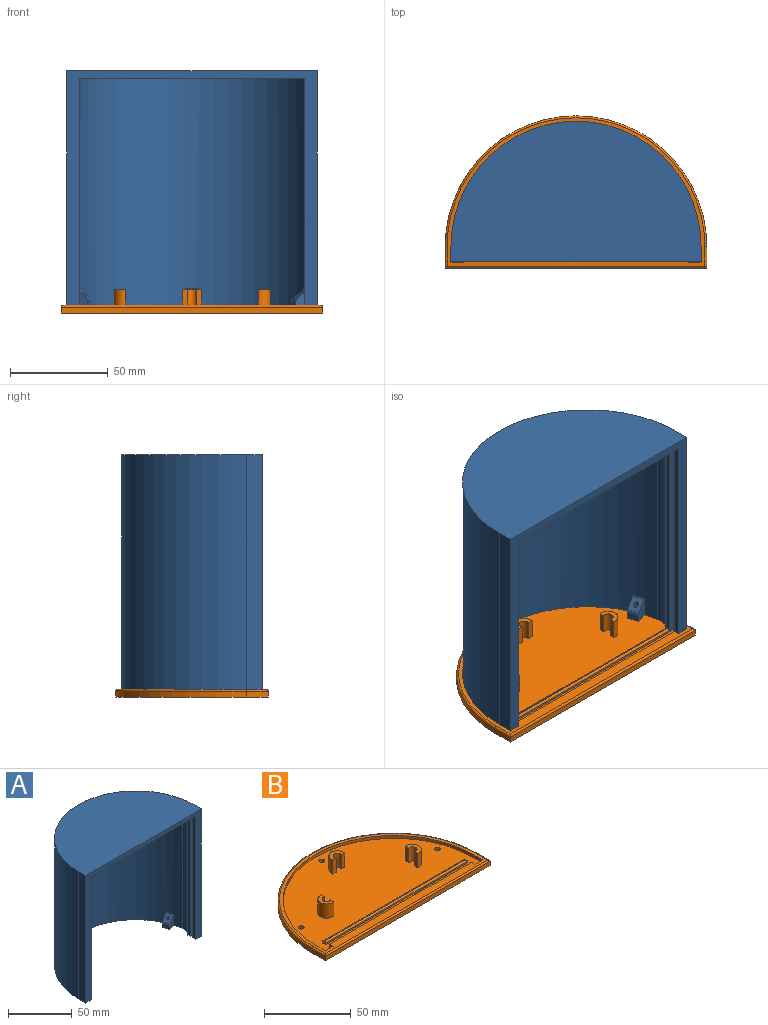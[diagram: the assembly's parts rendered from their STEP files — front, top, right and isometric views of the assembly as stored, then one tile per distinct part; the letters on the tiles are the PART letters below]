
ASSEMBLY  parts=2 mates=1
PART A: 43 faces, bbox 128x72x122 mm
  f0: plane 122.61x63.8mm, normal (0,0,-1), area 6215.1mm2, adj f4,f5,f6,f7,f8,f9,f10,f11
  f1: plane 115.5x3mm, normal (0,0,-1), area 346.5mm2, adj f2,f13,f14,f18
  f2: plane 118x3mm, normal (1,0,0), area 354mm2, adj f1,f13,f18,f20
  f3: plane 120x3.2mm, normal (1,0,0), area 384mm2, adj f11,f13,f20,f21
  f4: plane 118x2.33mm, normal (1,0,0), area 274.7mm2, adj f0,f5,f11,f20
  f5: plane 118x1.73mm, normal (0.78,0.62,0), area 261.1mm2, adj f0,f4,f6,f20
  f6: cylinder r=10mm len=118mm, axis (0,0,-1), area 986.5mm2, adj f0,f5,f7,f20
  f7: cylinder r=62mm len=122.34mm, axis (0,0,-1), area 20371.4mm2, adj f0,f6,f8,f20,f23,f25,f26,f28
  f8: cylinder r=10mm len=118mm, axis (0,0,-1), area 986.5mm2, adj f0,f7,f9,f20
  f9: plane 118x1.73mm, normal (-0.78,0.62,0), area 261.1mm2, adj f0,f8,f10,f20
  f10: plane 118x2.33mm, normal (-1,0,0), area 274.7mm2, adj f0,f9,f11,f20
  f11: plane 120.5x120mm, normal (0,-1,0), area 831mm2, adj f0,f3,f4,f10,f12,f20,f21
  f12: plane 120x3.2mm, normal (-1,0,0), area 384mm2, adj f11,f13,f20,f21
  f13: plane 120.5x120mm, normal (0,1,0), area 831mm2, adj f1,f2,f3,f12,f14,f20,f21
  f14: plane 118x3mm, normal (-1,0,0), area 354mm2, adj f1,f13,f18,f20
  f15: plane 122x8mm, normal (1,0,0), area 976mm2, adj f16,f18,f19,f20
  f16: cylinder r=64mm len=128mm, axis (0,0,-1), area 24529.6mm2, adj f15,f17,f19,f20
  f17: plane 122x8mm, normal (-1,0,0), area 976mm2, adj f16,f18,f19,f20
  f18: plane 128x122mm, normal (0,-1,0), area 1987mm2, adj f1,f2,f14,f15,f17,f19,f20
  f19: plane 128x72mm, normal (0,0,1), area 7458mm2, adj f15,f16,f17,f18
  f20: plane 128x72mm, normal (0,0,-1), area 623.9mm2, adj f2,f3,f4,f5,f6,f7,f8,f9
  f21: plane 120.5x3.2mm, normal (0,0,-1), area 385.6mm2, adj f3,f11,f12,f13
  f22: plane 7x4.16mm, normal (0,-1,0), area 28.6mm2, adj f20,f23,f25,f37
  f23: plane 10.48x5.92mm, normal (-1,0,0), area 44.4mm2, adj f7,f20,f22,f35,f37,f41
  f24: cylinder r=1.2mm len=8.5mm, axis (0,0,-1), area 57.5mm2, adj f20,f35
  f25: plane 10.48x5.92mm, normal (1,0,0), area 44.4mm2, adj f7,f20,f22,f35,f37,f41
  f26: plane 10.48x6.05mm, normal (0.34,-0.94,0), area 47mm2, adj f7,f20,f27,f34,f38,f40
  f27: plane 6.04x3.79mm, normal (-0.94,-0.34,0), area 23.9mm2, adj f20,f26,f28,f38
  f28: plane 10.48x6.04mm, normal (-0.34,0.94,0), area 47mm2, adj f7,f20,f27,f34,f38,f40
  f29: cylinder r=1.2mm len=8.5mm, axis (0,0,-1), area 56.7mm2, adj f20,f34
  f30: plane 6.58x4.36mm, normal (0.94,-0.34,0), area 29.2mm2, adj f20,f31,f33,f39
  f31: plane 10.48x5.77mm, normal (-0.34,-0.94,0), area 45.6mm2, adj f7,f20,f30,f36,f39,f42
  f32: cylinder r=1.2mm len=8.44mm, axis (0,0,-1), area 56.4mm2, adj f20,f36
  f33: plane 10.48x5.76mm, normal (0.34,0.94,0), area 45.6mm2, adj f7,f20,f30,f36,f39,f42
  f34: cone r=56mm half-angle=50.2deg, axis (0,0,1), area 41.6mm2, adj f26,f28,f29,f38,f40
  f35: cone r=56mm half-angle=50.2deg, axis (0,0,1), area 38.5mm2, adj f23,f24,f25,f37,f41
  f36: cone r=56mm half-angle=50.2deg, axis (0,0,1), area 45.6mm2, adj f31,f32,f33,f39,f42
  f37: bspline ~17.48x2.4mm, area 12.3mm2, adj f22,f23,f25,f35
  f38: bspline ~7.98x3.19mm, area 9mm2, adj f26,f27,f28,f34
  f39: bspline ~6.8x2.54mm, area 6mm2, adj f30,f31,f33,f36
  f40: torus R=61mm, axis (0,0,-1), area 5.6mm2, adj f7,f26,f28,f34
  f41: torus R=61mm, axis (0,0,-1), area 6.1mm2, adj f7,f23,f25,f35
  f42: torus R=61mm, axis (0,0,-1), area 6.1mm2, adj f7,f31,f33,f36
PART B: 46 faces, bbox 145x83.5x12 mm
  f0: plane 128x72mm, normal (0,0,1), area 6716.5mm2, adj f1,f2,f3,f10,f11,f12,f13,f14
  f1: cylinder r=1.6mm len=3.2mm, axis (0,0,-1), area 20.1mm2, adj f0,f9
  f2: cylinder r=1.6mm len=3.2mm, axis (0,0,-1), area 20.1mm2, adj f0,f9
  f3: cylinder r=1.6mm len=3.2mm, axis (0,0,-1), area 20.1mm2, adj f0,f9
  f4: plane 132x76mm, normal (0,0,1), area 1050.9mm2, adj f13,f14,f15,f16,f17,f18,f19,f21
  f5: plane 11x3mm, normal (1,0,0), area 33mm2, adj f6,f8,f9,f30
  f6: cylinder r=67mm len=134mm, axis (0,0,-1), area 631.5mm2, adj f5,f7,f9,f28
  f7: plane 11x3mm, normal (-1,0,0), area 33mm2, adj f6,f8,f9,f27
  f8: plane 134x3mm, normal (0,-1,0), area 402mm2, adj f5,f7,f9,f29
  f9: plane 134x78mm, normal (0,0,-1), area 8501.2mm2, adj f1,f2,f3,f5,f6,f7,f8
  f10: plane 115.5x1mm, normal (0,-1,0), area 115.5mm2, adj f0,f11,f20,f24
  f11: plane 2.33x1mm, normal (-1,0,0), area 2.3mm2, adj f0,f10,f12,f23
  f12: plane 115.5x1mm, normal (0,1,0), area 115.5mm2, adj f0,f11,f20,f25
  f13: plane 8x2mm, normal (-1,0,0), area 16mm2, adj f0,f4,f14,f21
  f14: cylinder r=64mm len=128mm, axis (0,0,1), area 402.1mm2, adj f0,f4,f13,f15
  f15: plane 8x2mm, normal (1,0,0), area 16mm2, adj f0,f4,f14,f16
  f16: plane 6.25x2mm, normal (0,1,0), area 12.5mm2, adj f0,f4,f15,f17
  f17: plane 3x2mm, normal (-1,0,0), area 6mm2, adj f0,f4,f16,f18
  f18: plane 115.5x2mm, normal (0,1,0), area 231mm2, adj f0,f4,f17,f19
  f19: plane 3x2mm, normal (1,0,0), area 6mm2, adj f0,f4,f18,f21
  f20: plane 2.33x1mm, normal (1,0,0), area 2.3mm2, adj f0,f10,f12,f26
  f21: plane 6.25x2mm, normal (0,1,0), area 12.5mm2, adj f0,f4,f13,f19
  f22: plane 113.5x0.33mm, normal (0,0,1), area 37.2mm2, adj f23,f24,f25,f26
  f23: cylinder r=1mm len=2.33mm, axis (0,-1,0), area 2.5mm2, adj f11,f22,f24,f25
  f24: cylinder r=1mm len=115.5mm, axis (1,0,0), area 180.3mm2, adj f10,f22,f23,f26
  f25: cylinder r=1mm len=115.5mm, axis (-1,0,0), area 180.3mm2, adj f12,f22,f23,f26
  f26: cylinder r=1mm len=2.33mm, axis (0,1,0), area 2.5mm2, adj f20,f22,f24,f25
  f27: cylinder r=1mm len=11mm, axis (0,1,0), area 16.7mm2, adj f4,f7,f28,f29
  f28: torus R=66mm, axis (0,0,1), area 328.8mm2, adj f4,f6,f27,f30
  f29: cylinder r=1mm len=134mm, axis (-1,0,0), area 209.3mm2, adj f4,f8,f27,f30
  f30: cylinder r=1mm len=11mm, axis (0,-1,0), area 16.7mm2, adj f4,f5,f28,f29
  f31: plane 10x2.55mm, normal (1,0,0), area 25.5mm2, adj f0,f32,f34,f35
  f32: cylinder r=5mm len=10mm, axis (0,0,-1), area 177.2mm2, adj f0,f31,f33,f35
  f33: plane 10x2.55mm, normal (1,0,0), area 25.5mm2, adj f0,f32,f34,f35
  f34: cylinder r=2.55mm len=10mm, axis (0,0,-1), area 100.7mm2, adj f0,f31,f33,f35
  f35: plane 10x6mm, normal (0,0,1), area 34mm2, adj f31,f32,f33,f34
  f36: cylinder r=5mm len=10mm, axis (0,0,-1), area 177.2mm2, adj f0,f37,f39,f40
  f37: plane 10x2.55mm, normal (0,-1,0), area 25.5mm2, adj f0,f36,f38,f40
  f38: cylinder r=2.55mm len=10mm, axis (0,0,-1), area 100.7mm2, adj f0,f37,f39,f40
  f39: plane 10x2.55mm, normal (0,-1,0), area 25.5mm2, adj f0,f36,f38,f40
  f40: plane 10x6mm, normal (0,0,1), area 34mm2, adj f36,f37,f38,f39
  f41: cylinder r=5mm len=10mm, axis (0,0,-1), area 177.2mm2, adj f0,f42,f44,f45
  f42: plane 10x2.55mm, normal (-1,0,0), area 25.5mm2, adj f0,f41,f43,f45
  f43: cylinder r=2.55mm len=10mm, axis (0,0,-1), area 100.7mm2, adj f0,f42,f44,f45
  f44: plane 10x2.55mm, normal (-1,0,0), area 25.5mm2, adj f0,f41,f43,f45
  f45: plane 10x6mm, normal (0,0,1), area 34mm2, adj f41,f42,f43,f44
PLACE A t=(3.73,25.94,24.18)mm
PLACE B t=(3.73,30.94,22.18)mm
MATE revolute B.f2 <-> A.f32  axis (0,0,1) through (-51.68,51.19,24.18)mm
